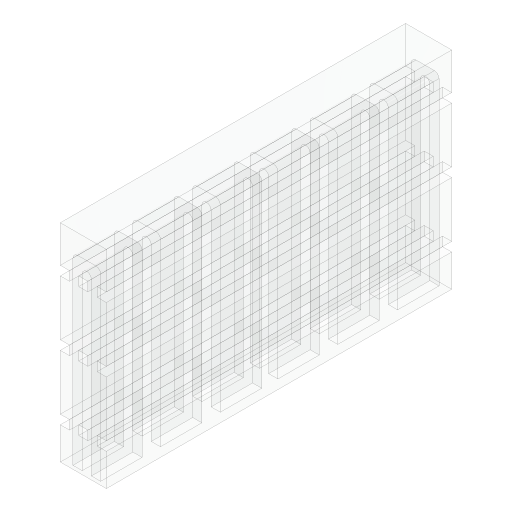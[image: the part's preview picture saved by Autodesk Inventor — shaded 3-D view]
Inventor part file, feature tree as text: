
AUTODESK INVENTOR PART (.ipt)
format: ipt  version: 2023 (Build 270158000, 158)  size: 562,176 bytes
history: native  units: mm
features: projected_geometry x13, extrude x5, sketch x5, fillet x3, plane x2
ambient origin geometry x8: Origin, YZ Plane, XZ Plane, XY Plane, X Axis, Y Axis, Z Axis, Center Point
bodies: 实体1 (feature_tree)
feature tree (28):
  extrude  "拉伸1"  Depth=750.0mm
  extrude  "拉伸2"  Depth=20.0mm
  plane  "工作平面1"
  extrude  "拉伸3"  Depth=97.5mm
  fillet  "圆角1"  Radius=20.0mm
  fillet  "圆角2"  Radius=20.0mm
  plane  "工作平面2"
  extrude  "拉伸4"  Depth=40.0mm
  fillet  "圆角3"  Radius=40.0mm
  extrude  "拉伸5"  [1 undecoded]
  sketch  "草图1"  dims[d0=100.0mm d1=750.0mm]
  sketch  "草图2"  dims[d2=450.0mm d3=0.0mm d4=20.0mm]
  projected_geometry  "投影回路1"
  sketch  "草图3"  dims[d5=90.0mm d6=97.5mm d7=20.0mm d8=20.0mm d9=90.0mm]
  projected_geometry  "投影回路2"
  projected_geometry  "投影回路3"
  projected_geometry  "投影回路4"
  projected_geometry  "投影回路5"
  projected_geometry  "投影回路6"
  projected_geometry  "投影回路7"
  sketch  "草图4"  dims[d10=20.0mm d11=90.0mm d12=40.0mm d13=40.0mm]
  projected_geometry  "投影回路8"
  projected_geometry  "投影回路9"
  projected_geometry  "投影回路10"
  projected_geometry  "投影回路11"
  projected_geometry  "投影回路12"
  projected_geometry  "投影回路13"
  sketch  "草图5"  dims[d14=400.0mm d15=0.0mm d16=-30.0mm d17=50.0mm d18=10.0mm d19=50.0mm d20=10.0mm d21=50.0mm d22=10.0mm d23=50.0mm d24=10.0mm d25=50.0mm d26=10.0mm d27=50.0mm d28=10.0mm d29=40.0mm d30=0.0mm d31=10.0mm d32=10.0mm d33=-40.0mm d34=90.0mm d35=20.0mm d36=90.0mm d37=20.0mm d38=90.0mm d39=20.0mm d40=90.0mm d41=20.0mm d42=90.0mm d43=20.0mm d44=90.0mm d45=20.0mm d46=20.0mm d47=0.0mm d48=10.0mm d49=20.0mm d50=20.0mm d51=20.0mm d52=20.0mm d53=20.0mm d54=20.0mm d55=120.0mm d56=120.0mm d57=20.0mm d58=20.0mm d59=20.0mm d60=20.0mm d61=20.0mm d62=20.0mm d63=20.0mm d64=20.0mm d65=20.0mm d66=20.0mm d67=20.0mm d68=20.0mm d69=750.0mm d70=0.0mm]
note: 1 required parameter value undecoded (feature->parameter linkage not recoverable at this tier; creation-order binding heuristic only, values carry confidence <= 0.55)
